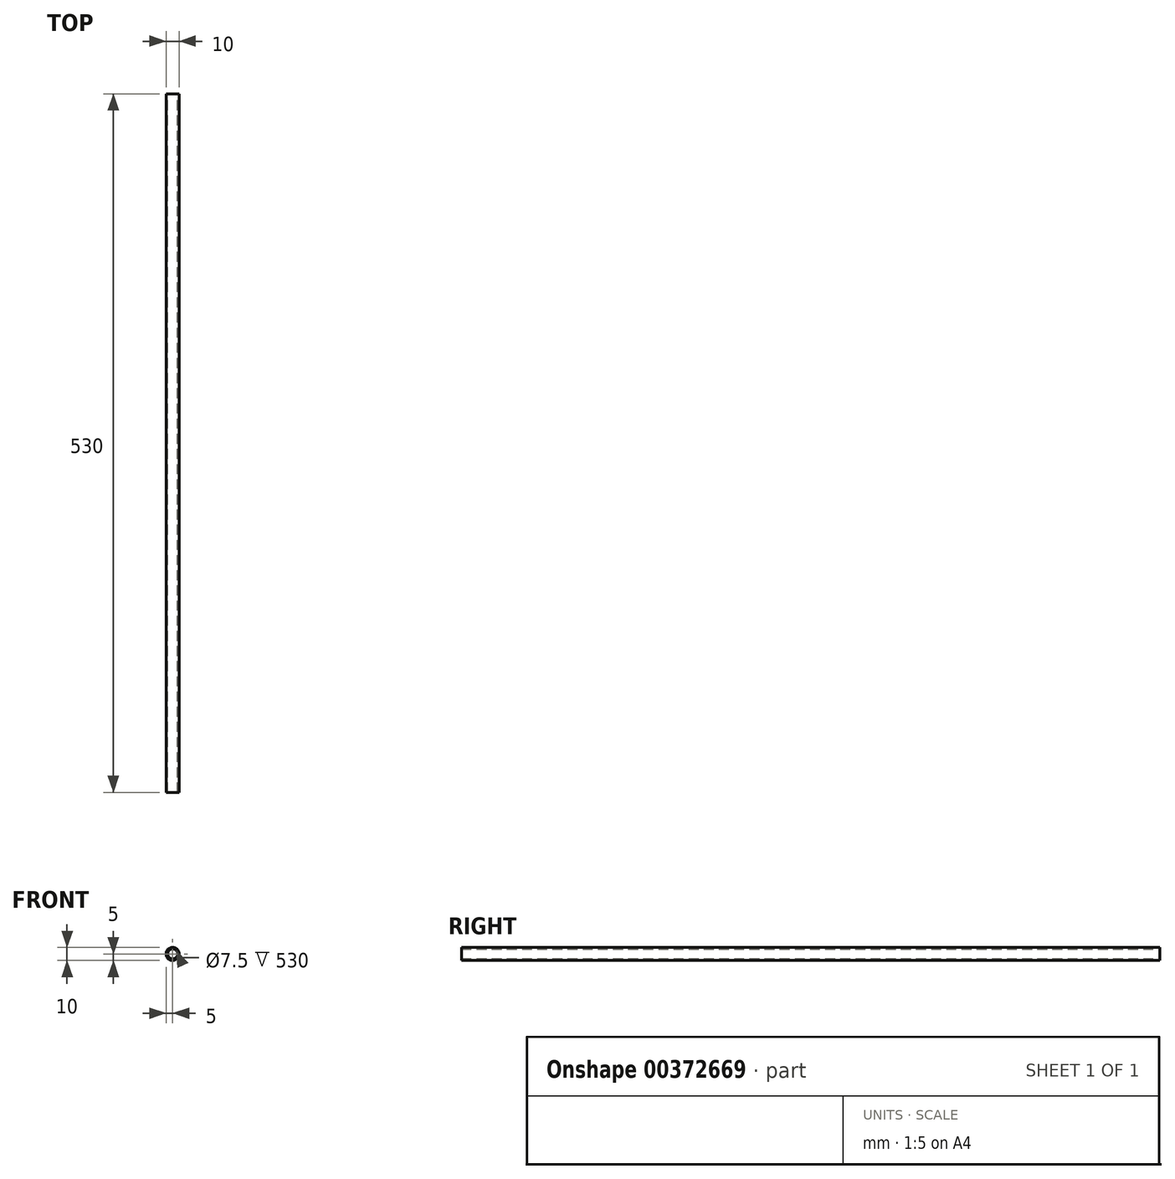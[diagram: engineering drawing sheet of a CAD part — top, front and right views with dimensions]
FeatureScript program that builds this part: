
annotation { "Feature Type Name" : "Feature", "Feature Type Description" : "" }
export const myFeature = defineFeature(function(context is Context, id is Id, definition is map)
    precondition{}
    {
        {
            var Q0;
            Q0=qCreatedBy(makeId("Front.planeOp"),FACE);
            var sketch = newSketch(context, id + "F0", { "sketchPlane" : qUnion([Q0])});
            skCircle(sketch, "E0", {"center": v(0, 0) * mm, "radius": 5 * mm});
            skCircle(sketch, "E1", {"center": v(0, 0) * mm, "radius": 3.75 * mm});
            skSolve(sketch);
        }
        {
            var Q0;
            Q0 = qSketchRegion(id + "F0", true);
            extrude(context, id + "F1", {"entities" : qUnion([Q0]), "depth" : 530 * mm, "offsetDistance" : 25 * mm});
        }
    });
